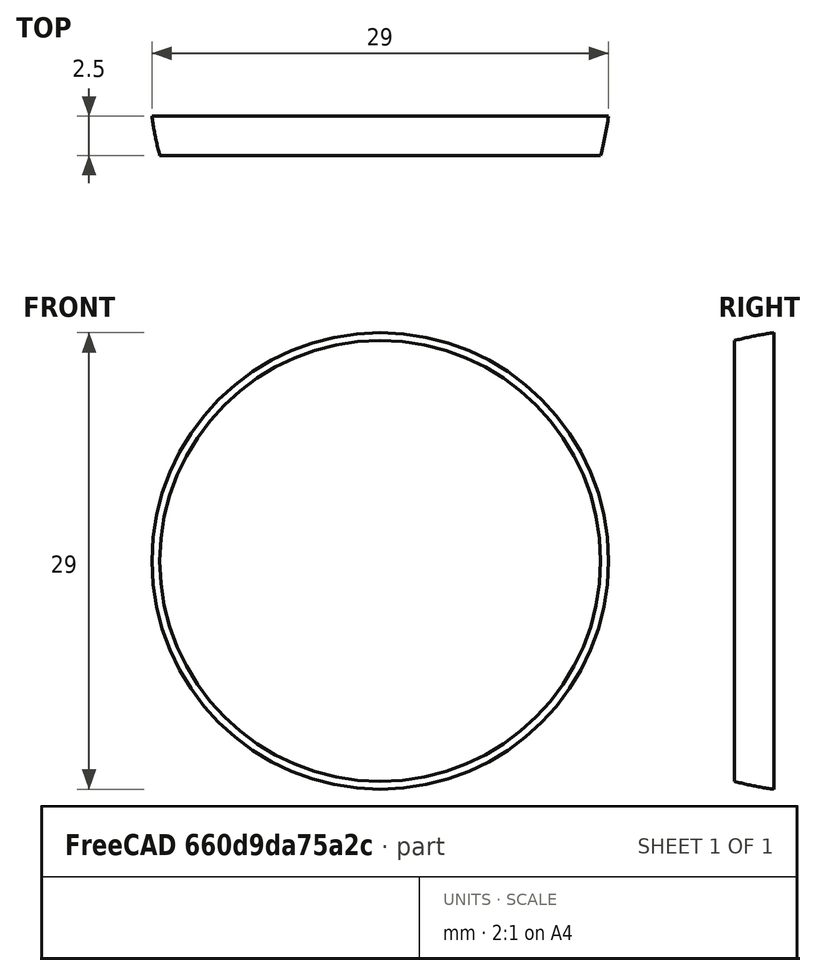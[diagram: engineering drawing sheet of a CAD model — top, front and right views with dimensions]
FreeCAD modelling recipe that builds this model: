
FCSTD DOCUMENT  (FreeCAD 0.18R4 (GitTag))
Label: Ariel Reciever Lid
License: All rights reserved
LicenseURL: http://en.wikipedia.org/wiki/All_rights_reserved
objects: Sketcher::SketchObject×1, PartDesign::Revolution×1, PartDesign::Body×1, Mesh::Feature×1
note: 4 computed .brp shape members not serialized (recipe doc carries the construction recipe); baked Part::Feature solids carry a one-line shape summary decoded from their .brp

FEATURE [Sketcher::SketchObject] Sketch
  MapMode = 5
  Support = -> [XY_Plane]
  sketch-geometry (4):
    g0: ArcOfCircle CenterX=-5.91732 CenterY=5.28346 CenterZ=0 NormalX=0 NormalY=0 NormalZ=1 AngleXU=0 Radius=20.6062 StartAngle=6.02389 EndAngle=6.14769
    g1: LineSegment StartX=14 StartY=-7.1e-15 StartZ=0 EndX=0 EndY=0 EndZ=0
    g2: LineSegment StartX=0 StartY=0 StartZ=0 EndX=0 EndY=2.5 EndZ=0
    g3: LineSegment StartX=0 StartY=2.5 StartZ=0 EndX=14.5 EndY=2.5 EndZ=0
  constraints (12):
    c: PointOnObject(g0,g-1)
    c: Coincident(g1,g0)
    c: Coincident(g1,g-1)
    c: PointOnObject(g2,g-2)
    c: Coincident(g2,g1)
    c: Coincident(g3,g2)
    c: Coincident(g3,g0)
    c: Horizontal(g3)
    c: DistanceX(g3,g3) = 14.5
    c: DistanceX(g1,g1) = 14
    c: DistanceY(g2,g2) = 2.5
    c: Radius(g0) = 20.6062
FEATURE [PartDesign::Revolution] Revolution
  Angle = 360
  Axis = (0,1,0)
  Base = (0,0,0)
  Profile = -> Sketch
  ReferenceAxis = -> Sketch [V_Axis]
  Reversed = true
FEATURE [PartDesign::Body] Body
  Group = -> [Sketch,Revolution]
  Origin = -> Origin
  Tip = -> Revolution
FEATURE [Mesh::Feature] Mesh  label="Body (Meshed)"
